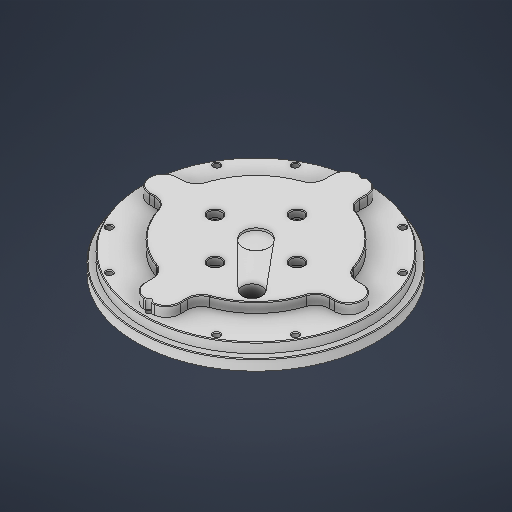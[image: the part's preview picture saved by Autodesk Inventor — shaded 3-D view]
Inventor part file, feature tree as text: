
AUTODESK INVENTOR PART (.ipt)
format: ipt  version: 2025 (Build 290162000, 162)  size: 489,984 bytes
history: native  units: in
note: dims shown in document units (in); Inventor stores cm internally (conversion verified against a paired STEP export)
features: sketch x14, extrude x9, hole x4, chamfer x3
ambient origin geometry x8: Origin, YZ Plane, XZ Plane, XY Plane, X Axis, Y Axis, Z Axis, Center Point
bodies: Solid1 (feature_tree)
feature tree (30):
  sketch  "Sketch1"  dims[d3=4.3307in d24=6.6535in]
  extrude  "Extrusion1"  Depth=6.6535in
  extrude  "Extrusion2"  Depth=5.9843in
  extrude  "Extrusion3"  Depth=4.3307in
  sketch  "Sketch2"  dims[d27=0.9843in d28=4.3307in]
  extrude  "Extrusion4"  Depth=0.3937in
  hole  "Hole1"  [1 undecoded]
  hole  "Hole2"  [1 undecoded]
  sketch  "Sketch4"  dims[d38=0.2953in d39=0.0in d40=2.2835in]
  extrude  "Extrusion5"  Depth=2.2835in
  extrude  "Extrusion6"  Depth=0.1969in
  hole  "Hole3"  [1 undecoded]
  chamfer  "Chamfer1"  Distance=0.7874in Angle=360.0deg
  chamfer  "Chamfer2"  Distance=0.1969in
  hole  "Hole5"  [1 undecoded]
  extrude  "Extrusion9"  Depth=0.0591in TaperAngle=0.0deg
  extrude  "Extrusion10"  Depth=0.0197in TaperAngle=0.0deg
  chamfer  "Chamfer4"  Distance=0.1969in
  extrude  "Extrusion11"  Depth=0.0197in TaperAngle=360.0deg
  sketch  "Sketch Circular Pattern1"  dims[d25=6.2992in d26=5.9843in]
  sketch  "Sketch3"  dims[d31=0.3937in d32=0.3937in]
  sketch  "Sketch Circular Pattern2"  dims[d29=0.7874in d30=0.3937in]
  sketch  "Sketch5"  dims[d41=0.3543in d42=0.1969in]
  sketch  "Sketch Circular Pattern3"  dims[d34=0.8465in d35=0.0in d36=0.5709in d37=0.0in]
  sketch  "Sketch7"  dims[d56=5.9843in]
  sketch  "Sketch Circular Pattern5"  dims[d43=1.5748in d45=360.0deg d47=0.1969in d48=0.0in]
  sketch  "Sketch9"  dims[d57=0.1378in d58=0.7874in d60=360.0deg]
  sketch  "Sketch Circular Pattern6"  dims[d49=0.2165in d50=0.7874in d51=0.1575in d52=0.0787in d53=90.0deg d54=0.315in d55=0.8108in]
  sketch  "Sketch10"  dims[d62=0.1276in d63=1.0025in d64=0.1575in d65=0.2756in d66=90.0deg d67=0.4646in d68=0.0in]
  sketch  "Sketch11"  dims[d69=3.2283in d70=0.1969in d71=0.7874in d72=0.0591in d73=0.0in d74=0.4724in d75=0.0in d76=0.1969in d77=4.7244in d79=360.0deg d81=0.1628in d82=0.7874in d83=0.1575in d84=0.0787in d85=90.0deg d86=0.3937in d87=0.8108in d88=0.0197in d89=0.0787in d90=45.0deg d91=0.0197in d92=0.0787in d93=45.0deg d107=3.7402in d108=0.1969in d109=6.2992in d111=360.0deg d113=0.1969in d114=0.7874in d115=0.748in d116=0.3543in d117=90.0deg d118=0.7874in d119=0.8108in d139=0.7185in d140=3.1496in d141=0.7185in d142=3.1496in d144=360.0deg d146=0.0591in d147=0.0in d151=0.5512in d152=1.7717in d153=0.0in d154=0.0in d155=0.0197in d156=0.0787in d157=45.0deg d158=0.5512in d159=1.7717in d160=0.0394in d161=0.0in d162=0.1969in d137=0.0197in d138=0.0344in]
note: 4 required parameter values undecoded (feature->parameter linkage not recoverable at this tier; creation-order binding heuristic only, values carry confidence <= 0.55)
